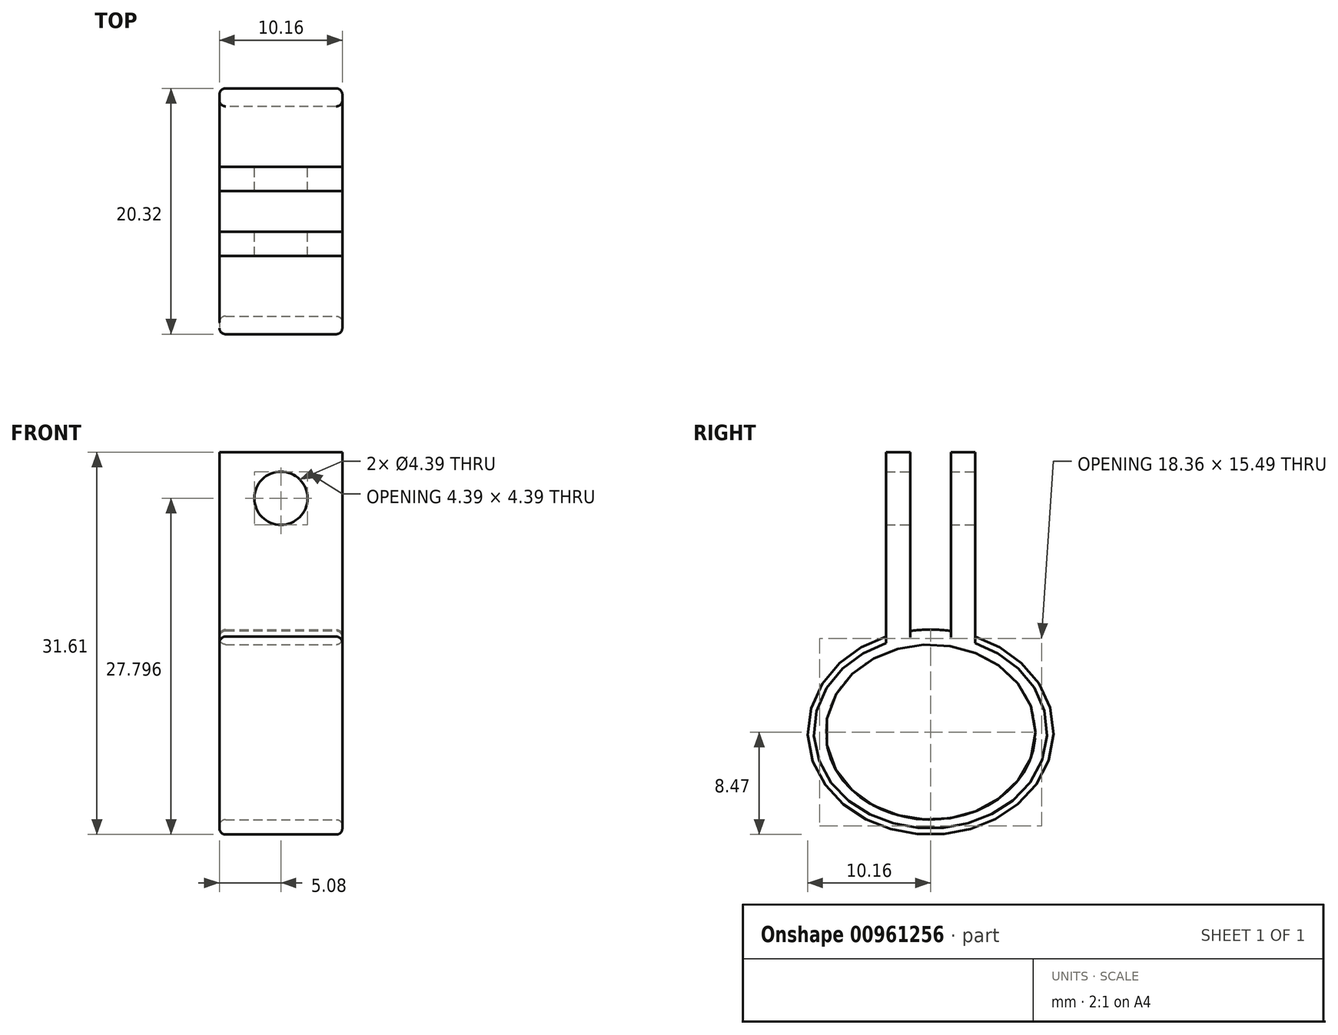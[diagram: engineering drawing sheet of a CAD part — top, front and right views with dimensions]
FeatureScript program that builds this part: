
annotation { "Feature Type Name" : "Feature", "Feature Type Description" : "" }
export const myFeature = defineFeature(function(context is Context, id is Id, definition is map)
    precondition{}
    {
        {
            var Q0;
            Q0=qCreatedBy(makeId("Right.planeOp"),FACE);
            var sketch = newSketch(context, id + "F0", { "sketchPlane" : qUnion([Q0])});
            skEllipse(sketch, "E0", {"center": v(0, 0) * mm, "majorRadius": 8.67 * mm, "minorRadius": 7.24 * mm, "majorAxis": v(1, 0)});
            skEllipse(sketch, "E1", {"center": v(0, 0) * mm, "majorRadius": 10.16 * mm, "minorRadius": 8.47 * mm, "majorAxis": v(1, 0)});
            skSolve(sketch);
        }
        {
            var Q0;
            Q0=makeQuery(id+"F0.imprint","IMPRINT",FACE,{"disambiguationData":[TD([[makeQuery(id+"F0.imprint","IMPRINT",EDGE,{"derivedFrom":sQuery(id+"F0.wireOp",EDGE,"E0")}),-1.0]])]});
            extrude(context, id + "F1", {"entities" : qUnion([Q0]), "depth" : 10.16 * mm, "offsetDistance" : 25.4 * mm});
        }
        {
            var Q0;
            Q0=makeQuery(id+"F1.opExtrude","CAP_FACE",FACE,{"disambiguationData":[OSD([sQuery(id+"F0.wireOp",EDGE,"E0"),sQuery(id+"F0.wireOp",EDGE,"E1")])],"isStart":false});
            var sketch = newSketch(context, id + "F2", { "sketchPlane" : qUnion([Q0])});
            skLineSegment(sketch, "E2", {"start": v(-3.68, 7.9) * mm, "end": v(-3.68, 23.14) * mm});
            skLineSegment(sketch, "E3", {"start": v(-3.68, 23.14) * mm, "end": v(-1.68, 23.14) * mm});
            skLineSegment(sketch, "E4", {"start": v(-1.68, 23.14) * mm, "end": v(-1.68, 8.35) * mm});
            skLineSegment(sketch, "E5", {"start": v(0, 7.97) * mm, "end": v(0, 12.7) * mm, "construction": true});
            skLineSegment(sketch, "E6.MirrorCS", {"start": v(1.68, 23.14) * mm, "end": v(1.68, 8.35) * mm});
            skLineSegment(sketch, "E7.MirrorCS", {"start": v(3.68, 23.14) * mm, "end": v(1.68, 23.14) * mm});
            skLineSegment(sketch, "E8.MirrorCS", {"start": v(3.68, 7.9) * mm, "end": v(3.68, 23.14) * mm});
            skSolve(sketch);
        }
        {
            var Q0;
            {var subQ0=sQuery(id+"F2.wireOp",EDGE,"E2");Q0=makeQuery(id+"F2.imprint","IMPRINT",FACE,{"disambiguationData":[TD([[makeQuery(id+"F2.imprint","IMPRINT",EDGE,{"derivedFrom":subQ0}),-1.0]])]});}
            var Q1;
            {var subQ0=sQuery(id+"F2.wireOp",EDGE,"E6.MirrorCS");Q1=makeQuery(id+"F2.imprint","IMPRINT",FACE,{"disambiguationData":[TD([[makeQuery(id+"F2.imprint","IMPRINT",EDGE,{"derivedFrom":subQ0}),1.0]])]});}
            extrude(context, id + "F3", {"entities" : qUnion([Q0, Q1]), "operationType" : NewBodyOperationType.ADD, "oppositeDirection" : true, "depth" : 10.16 * mm, "offsetDistance" : 25.4 * mm});
        }
        {
            var Q0;
            Q0=makeQuery(id+"F3.opExtrude","SWEPT_FACE",FACE,{"disambiguationData":[OSD([sQuery(id+"F2.wireOp",EDGE,"E8.MirrorCS")])]});
            var sketch = newSketch(context, id + "F4", { "sketchPlane" : qUnion([Q0])});
            skCircle(sketch, "E9", {"center": v(-5.08, 19.33) * mm, "radius": 2.2 * mm});
            skLineSegment(sketch, "E10", {"start": v(-5.08, 23.14) * mm, "end": v(-5.08, 7.9) * mm, "construction": true});
            skSolve(sketch);
        }
        {
            var Q0;
            Q0=makeQuery(id+"F4.imprint","IMPRINT",FACE,{"disambiguationData":[TD([[makeQuery(id+"F4.imprint","IMPRINT",EDGE,{"derivedFrom":sQuery(id+"F4.wireOp",EDGE,"E9")}),1.0]])]});
            extrude(context, id + "F5", {"entities" : qUnion([Q0]), "operationType" : NewBodyOperationType.REMOVE, "oppositeDirection" : true, "depth" : 25.4 * mm, "offsetDistance" : 25.4 * mm});
        }
        {
            var Q0;
            Q0=makeQuery(id+"F1.opExtrude","CAP_EDGE",EDGE,{"disambiguationData":[OSD([sQuery(id+"F0.wireOp",EDGE,"E0")])],"isStart":false});
            var Q1;
            Q1=makeQuery(id+"F1.opExtrude","CAP_EDGE",EDGE,{"disambiguationData":[OSD([sQuery(id+"F0.wireOp",EDGE,"E1")])],"isStart":false});
            var Q2;
            Q2=makeQuery(id+"F1.opExtrude","CAP_EDGE",EDGE,{"disambiguationData":[OSD([sQuery(id+"F0.wireOp",EDGE,"E1")])],"isStart":true});
            var Q3;
            Q3=makeQuery(id+"F1.opExtrude","CAP_EDGE",EDGE,{"disambiguationData":[OSD([sQuery(id+"F0.wireOp",EDGE,"E0")])],"isStart":true});
            fillet(context, id + "F6", {"entities" : qUnion([Q0, Q1, Q2, Q3]), "radius" : 0.5 * mm, "tangentPropagation" : true, "allowEdgeOverflow" : false});
        }
    });
